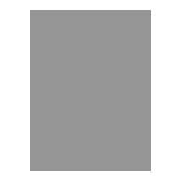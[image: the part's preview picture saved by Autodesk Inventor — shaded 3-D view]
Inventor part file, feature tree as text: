
AUTODESK INVENTOR PART (.ipt)
format: ipt  version: 2019.4 (Build 234330000, 330)  size: 114,688 bytes
history: native  units: mm (DEFAULTED — no unit token found)
features: other x4, plane x3, split x2, sketch x2
ambient origin geometry x8: Origin, YZ Plane, XZ Plane, XY Plane, X Axis, Y Axis, Z Axis, Center Point
bodies: Solid1 (feature_tree), Body (feature_tree)
feature tree (11):
  parser-record x1  (decoder bookkeeping rows leaked as tree rows — omitted from the tree; the rows remain in map.json)
  other  "Driven Length"
  other  "Start plane"
  other  "End plane"
  plane  "Work Plane5"
  split  "Split2"
  plane  "Work Plane6"
  split  "Split3"
  sketch  "Sketch3"  dims[d0=12.7mm]
  plane  "Work Plane3"
  sketch  "Sketch4"  dims[d1=12.7mm d2=112.141126mm d3=0.0mm d4=6.35mm d5=6.35mm d6=6.35mm d7=118.491126mm d8=90.0deg d9=112.141126mm]
